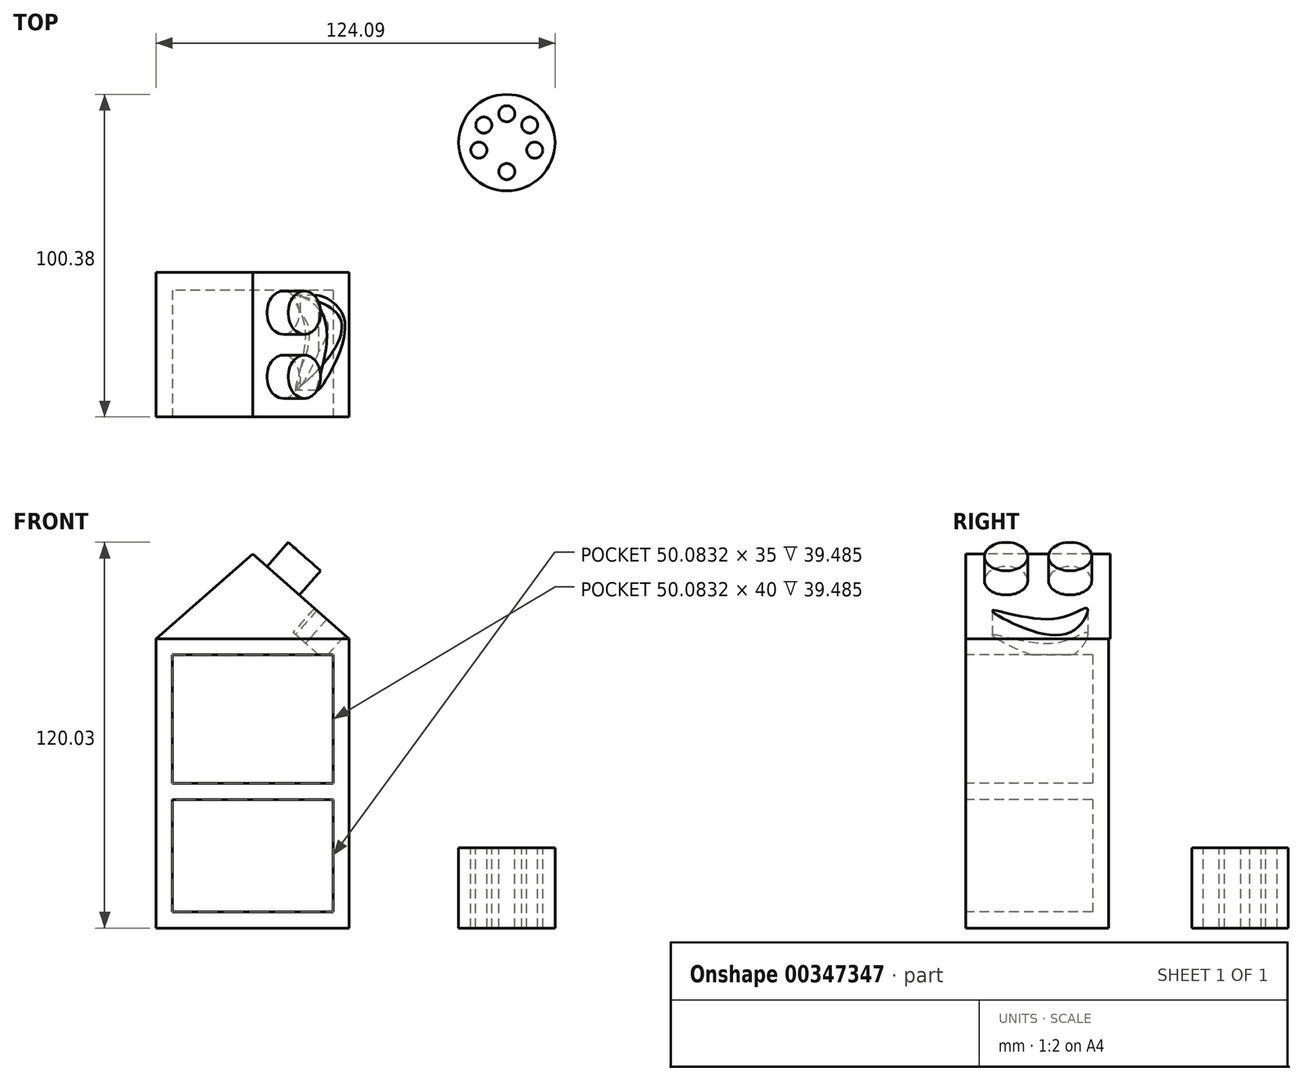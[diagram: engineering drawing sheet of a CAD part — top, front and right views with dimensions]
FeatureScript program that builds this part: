
annotation { "Feature Type Name" : "Feature", "Feature Type Description" : "" }
export const myFeature = defineFeature(function(context is Context, id is Id, definition is map)
    precondition{}
    {
        {
            var Q0;
            Q0=qCreatedBy(makeId("Top.planeOp"),FACE);
            var sketch = newSketch(context, id + "F0", { "sketchPlane" : qUnion([Q0])});
            skCircle(sketch, "E0", {"center": v(0, 0) * mm, "radius": 15 * mm});
            skSolve(sketch);
        }
        {
            var Q0;
            Q0 = qSketchRegion(id + "F0", true);
            extrude(context, id + "F1", {"entities" : qUnion([Q0]), "depth" : 25 * mm});
        }
        {
            var Q0;
            Q0=makeQuery(id+"F1.opExtrude","CAP_FACE",FACE,{"disambiguationData":[OSD([sQuery(id+"F0.wireOp",EDGE,"E0")])],"isStart":false});
            var sketch = newSketch(context, id + "F2", { "sketchPlane" : qUnion([Q0])});
            skLineSegment(sketch, "E1", {"start": v(0, 15) * mm, "end": v(0, 9) * mm, "construction": true});
            skLineSegment(sketch, "E2", {"start": v(12, 9) * mm, "end": v(0, 9) * mm, "construction": true});
            skCircle(sketch, "E3", {"center": v(0, 9) * mm, "radius": 2.5 * mm});
            skCircle(sketch, "E4.1.0", {"center": v(7.14, 5.48) * mm, "radius": 2.5 * mm});
            skCircle(sketch, "E4.2.0", {"center": v(8.7, -2.33) * mm, "radius": 2.5 * mm});
            skPoint(sketch, "E4.center", {"position": v(0, 0) * mm});
            skLineSegment(sketch, "E4.anchor1", {"start": v(0, 0) * mm, "end": v(0, 9) * mm, "construction": true});
            skLineSegment(sketch, "E4.anchor2", {"start": v(0, 0) * mm, "end": v(8.7, -2.33) * mm, "construction": true});
            skCircle(sketch, "E5.1.0", {"center": v(0, -9) * mm, "radius": 2.5 * mm});
            skCircle(sketch, "E5.2.0", {"center": v(-8.7, -2.33) * mm, "radius": 2.5 * mm});
            skLineSegment(sketch, "E5.anchor2", {"start": v(0, 0) * mm, "end": v(-8.7, -2.33) * mm, "construction": true});
            skCircle(sketch, "E6.1.0", {"center": v(-7.14, 5.48) * mm, "radius": 2.5 * mm});
            skSolve(sketch);
        }
        {
            var Q0;
            Q0 = qSketchRegion(id + "F2", true);
            extrude(context, id + "F3", {"entities" : qUnion([Q0]), "operationType" : NewBodyOperationType.REMOVE, "oppositeDirection" : true, "depth" : 25 * mm});
        }
        {
            var Q0;
            Q0=qCreatedBy(makeId("Top.planeOp"),FACE);
            var sketch = newSketch(context, id + "F4", { "sketchPlane" : qUnion([Q0])});
            skLineSegment(sketch, "E7.bottom", {"start": v(-49.01, -40.9) * mm, "end": v(-109.1, -40.9) * mm});
            skLineSegment(sketch, "E7.top", {"start": v(-49.01, -85.38) * mm, "end": v(-109.1, -85.38) * mm});
            skLineSegment(sketch, "E7.left", {"start": v(-49.01, -40.9) * mm, "end": v(-49.01, -85.38) * mm});
            skLineSegment(sketch, "E7.right", {"start": v(-109.1, -40.9) * mm, "end": v(-109.1, -85.38) * mm});
            skSolve(sketch);
        }
        {
            var Q0;
            Q0 = qSketchRegion(id + "F4", true);
            extrude(context, id + "F5", {"entities" : qUnion([Q0]), "depth" : 45 * mm});
        }
        {
            var Q0;
            Q0=makeQuery(id+"F5.opExtrude","SWEPT_FACE",FACE,{"disambiguationData":[OSD([sQuery(id+"F4.wireOp",EDGE,"E7.top")])]});
            shell(context, id + "F6", {"entities" : qUnion([Q0]), "thickness" : 5 * mm});
        }
        {
            var Q0;
            Q0=makeQuery(id+"F5.opExtrude","CAP_FACE",FACE,{"disambiguationData":[OSD([sQuery(id+"F4.wireOp",EDGE,"E7.bottom"),sQuery(id+"F4.wireOp",EDGE,"E7.top"),sQuery(id+"F4.wireOp",EDGE,"E7.left"),sQuery(id+"F4.wireOp",EDGE,"E7.right")])],"isStart":false});
            var sketch = newSketch(context, id + "F7", { "sketchPlane" : qUnion([Q0])});
            skLineSegment(sketch, "E8.bottom", {"start": v(-109.1, -85.38) * mm, "end": v(-49.01, -85.38) * mm});
            skLineSegment(sketch, "E8.top", {"start": v(-109.1, -40.9) * mm, "end": v(-49.01, -40.9) * mm});
            skLineSegment(sketch, "E8.left", {"start": v(-109.1, -85.38) * mm, "end": v(-109.1, -40.9) * mm});
            skLineSegment(sketch, "E8.right", {"start": v(-49.01, -85.38) * mm, "end": v(-49.01, -40.9) * mm});
            skSolve(sketch);
        }
        {
            var Q0;
            Q0 = qSketchRegion(id + "F7", true);
            extrude(context, id + "F8", {"entities" : qUnion([Q0]), "operationType" : NewBodyOperationType.ADD, "depth" : 45 * mm});
        }
        {
            var Q0;
            Q0=makeQuery(id+"F8.boolean.opBoolean","MERGE",FACE,{"derivedFrom":[makeQuery(id+"F5.opExtrude","SWEPT_FACE",FACE,{"disambiguationData":[OSD([sQuery(id+"F4.wireOp",EDGE,"E7.top")])]}),makeQuery(id+"F8.opExtrude","SWEPT_FACE",FACE,{"disambiguationData":[OSD([sQuery(id+"F7.wireOp",EDGE,"E8.bottom")])]})]});
            shell(context, id + "F9", {"entities" : qUnion([Q0]), "thickness" : 5 * mm});
        }
        {
            var Q0;
            Q0=makeQuery(id+"F8.boolean.opBoolean","MERGE",FACE,{"derivedFrom":[makeQuery(id+"F5.opExtrude","SWEPT_FACE",FACE,{"disambiguationData":[OSD([sQuery(id+"F4.wireOp",EDGE,"E7.top")])]}),makeQuery(id+"F8.opExtrude","SWEPT_FACE",FACE,{"disambiguationData":[OSD([sQuery(id+"F7.wireOp",EDGE,"E8.bottom")])]})]});
            var sketch = newSketch(context, id + "F10", { "sketchPlane" : qUnion([Q0])});
            skLineSegment(sketch, "E9", {"start": v(-109.1, 90) * mm, "end": v(-79.05, 116.41) * mm});
            skLineSegment(sketch, "E10", {"start": v(-49.01, 90) * mm, "end": v(-79.05, 116.41) * mm});
            skSolve(sketch);
        }
        {
            var Q0;
            Q0=makeQuery(id+"F10.imprint","IMPRINT",FACE,{"disambiguationData":[TD([[makeQuery(id+"F10.imprint","IMPRINT",EDGE,{"derivedFrom":sQuery(id+"F10.wireOp",EDGE,"E9")}),-1.0]])]});
            extrude(context, id + "F11", {"entities" : qUnion([Q0]), "oppositeDirection" : true, "depth" : 45 * mm});
        }
        {
            var Q0;
            Q0=makeQuery(id+"F11.opExtrude","SWEPT_FACE",FACE,{"disambiguationData":[OSD([sQuery(id+"F10.wireOp",EDGE,"E10")])]});
            var sketch = newSketch(context, id + "F12", { "sketchPlane" : qUnion([Q0])});
            skCircle(sketch, "E11", {"center": v(-123.62, -72.85) * mm, "radius": 6.72 * mm});
            skLineSegment(sketch, "E12", {"start": v(-136.23, -62.88) * mm, "end": v(-96.23, -62.88) * mm, "construction": true});
            skCircle(sketch, "E13.MirrorC", {"center": v(-123.62, -52.92) * mm, "radius": 6.72 * mm});
            skSolve(sketch);
        }
        {
            var Q0;
            Q0 = qSketchRegion(id + "F12", true);
            extrude(context, id + "F13", {"entities" : qUnion([Q0]), "operationType" : NewBodyOperationType.ADD, "depth" : 10 * mm});
        }
        {
            var Q0;
            Q0=makeQuery(id+"F11.opExtrude","SWEPT_FACE",FACE,{"disambiguationData":[OSD([sQuery(id+"F10.wireOp",EDGE,"E10")])]});
            var sketch = newSketch(context, id + "F14", { "sketchPlane" : qUnion([Q0])});
            skFitSpline(sketch, "E14", {"points": [v(-109.6, -77) * mm, v(-105.68, -57.76) * mm, v(-110.57, -47.67) * mm, v(-99.66, -52.36) * mm, v(-102.13, -68.6) * mm, v(-109.6, -77) * mm]});
            skSolve(sketch);
        }
        {
            var Q0;
            Q0 = qSketchRegion(id + "F14", true);
            extrude(context, id + "F15", {"entities" : qUnion([Q0]), "operationType" : NewBodyOperationType.REMOVE, "oppositeDirection" : true, "depth" : 10 * mm});
        }
    });
